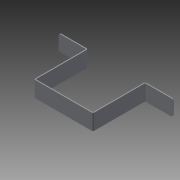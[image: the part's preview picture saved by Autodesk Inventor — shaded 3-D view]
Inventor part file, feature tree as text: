
AUTODESK INVENTOR PART (.ipt)
format: ipt  version: 2014 SP1 (Build 180222100, 222)  size: 130,048 bytes
history: native  units: in
note: dims shown in document units (in); Inventor stores cm internally (conversion verified against a paired STEP export)
features: sheet_metal_op x7, sketch x3, other x3, chamfer x1
ambient origin geometry x8: Origin, YZ Plane, XZ Plane, XY Plane, X Axis, Y Axis, Z Axis, Center Point
bodies: Solid1 (feature_tree)
feature tree (14):
  sheet_metal_op  "Face1"
  sheet_metal_op  "Flange1"
  sheet_metal_op  "Flange2"
  chamfer  "Corner Round1"
  sketch  "Sketch1"  dims[d0=7.25in]
  other  "Plate1"
  sketch  "Sketch2"  dims[d1=2.0in]
  other  "Plate2"
  sheet_metal_op  "Bend1"
  sheet_metal_op  "Corner1"
  sketch  "Sketch3"  dims[d2=0.12in d3=0.12in d4=0.06in d5=0.24in d6=0.12in d7=6.5in d8=90.0deg d9=0.05in d10=0.48in d11=0.12in d12=0.12in d13=0.12in d14=0.06in d15=0.24in d16=0.12in d17=3.5in d18=90.0deg d19=0.05in d20=0.48in d21=0.12in d22=0.12in d23=0.25in]
  other  "Plate3"
  sheet_metal_op  "Bend2"
  sheet_metal_op  "Corner2"
